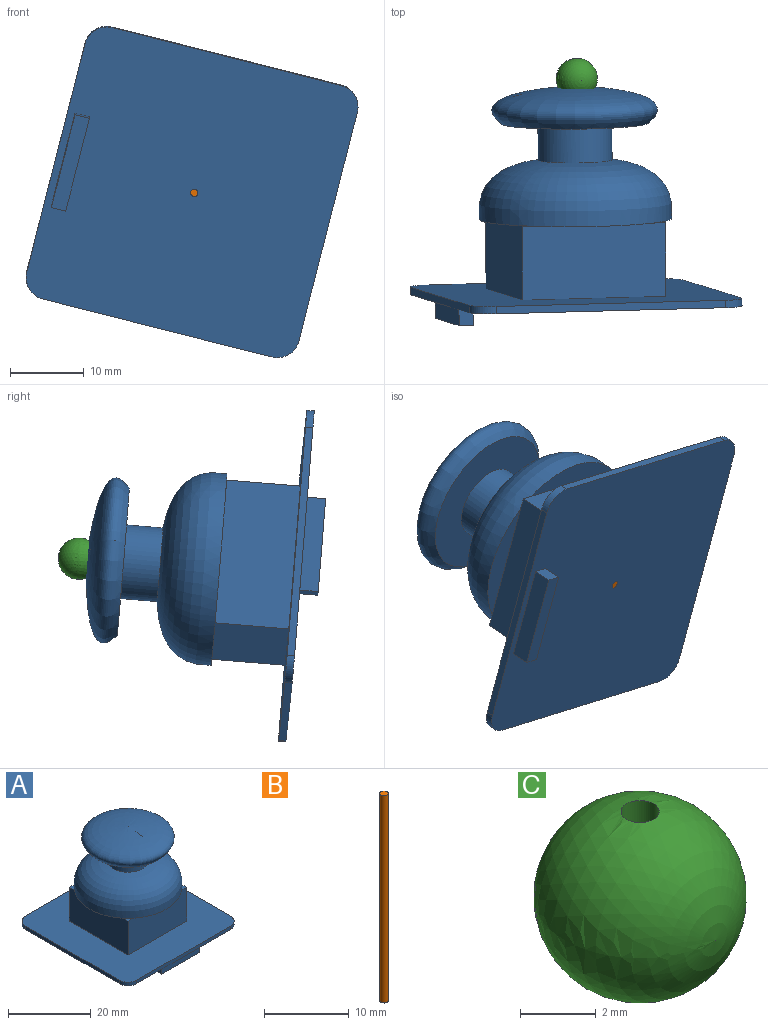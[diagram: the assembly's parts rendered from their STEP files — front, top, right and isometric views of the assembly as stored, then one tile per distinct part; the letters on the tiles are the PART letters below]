
ASSEMBLY  parts=3 mates=2
PART A: 31 faces, bbox 38x38x31.5 mm
  f0: plane 1.69x1.69mm, normal (0,0,1), area 1.3mm2, adj f19,f20,f26
  f1: plane 1.69x1.69mm, normal (0,0,1), area 1.3mm2, adj f20,f21,f26
  f2: plane 1.69x1.69mm, normal (0,0,1), area 1.3mm2, adj f18,f21,f26
  f3: plane 38x38mm, normal (0,0,-1), area 1410.3mm2, adj f4,f5,f6,f7,f9,f10,f11,f12
  f4: plane 32x1mm, normal (0,-1,0), area 32mm2, adj f3,f8,f9,f12
  f5: plane 32x1mm, normal (1,0,0), area 32mm2, adj f3,f8,f9,f10
  f6: plane 32x1mm, normal (0,1,0), area 32mm2, adj f3,f8,f10,f11
  f7: plane 32x1mm, normal (-1,0,0), area 32mm2, adj f3,f8,f11,f12
  f8: plane 38x38mm, normal (0,0,1), area 1036.3mm2, adj f4,f5,f6,f7,f9,f10,f11,f12
  f9: cylinder r=3mm len=3mm, axis (0,0,-1), area 4.7mm2, adj f3,f4,f5,f8
  f10: cylinder r=3mm len=3mm, axis (0,0,1), area 4.7mm2, adj f3,f5,f6,f8
  f11: cylinder r=3mm len=3mm, axis (0,0,-1), area 4.7mm2, adj f3,f6,f7,f8
  f12: cylinder r=3mm len=3mm, axis (0,0,1), area 4.7mm2, adj f3,f4,f7,f8
  f13: plane 13x2.5mm, normal (0,-1,0), area 32.5mm2, adj f3,f14,f16,f17
  f14: plane 2.5x2mm, normal (1,0,0), area 5mm2, adj f3,f13,f15,f17
  f15: plane 13x2.5mm, normal (0,1,0), area 32.5mm2, adj f3,f14,f16,f17
  f16: plane 2.5x2mm, normal (-1,0,0), area 5mm2, adj f3,f13,f15,f17
  f17: plane 13x2mm, normal (0,0,-1), area 26mm2, adj f13,f14,f15,f16
  f18: plane 20x10mm, normal (0,-1,0), area 200mm2, adj f2,f8,f19,f21,f22,f23
  f19: plane 20x10mm, normal (1,0,0), area 200mm2, adj f0,f8,f18,f20,f22,f24
  f20: plane 20x10mm, normal (0,1,0), area 200mm2, adj f0,f1,f8,f19,f21,f25
  f21: plane 20x10mm, normal (-1,0,0), area 200mm2, adj f1,f2,f8,f18,f20,f27
  f22: plane 1.69x1.69mm, normal (0,0,1), area 1.3mm2, adj f18,f19,f26
  f23: plane 16.61x3mm, normal (0,0,-1), area 34.1mm2, adj f18,f26
  f24: plane 16.61x3mm, normal (0,0,-1), area 34.1mm2, adj f19,f26
  f25: plane 16.61x3mm, normal (0,0,-1), area 34.1mm2, adj f20,f26
  f26: revolved ~26.01x26.01mm, area 834.5mm2, adj f0,f1,f2,f22,f23,f24,f25,f27
  f27: plane 16.61x3mm, normal (0,0,-1), area 34.1mm2, adj f21,f26
  f28: revolved ~22.43x22.43mm, area 610.2mm2, adj f29
  f29: plane 20x20mm, normal (0,0,-1), area 235.6mm2, adj f28,f30
  f30: cylinder r=5mm len=10mm, axis (0,0,1), area 157.1mm2, adj f26,f29
PART B: 3 faces, bbox 1x1x30 mm
  f0: cylinder r=0.5mm len=30mm, axis (0,0,-1), area 94.2mm2, adj f1,f2
  f1: plane 1x1mm, normal (0,0,1), area 0.8mm2, adj f0
  f2: plane 1x1mm, normal (0,0,-1), area 0.8mm2, adj f0
PART C: 2 faces, bbox 5.6x5.6x5.6 mm
  f0: sphere r=2.8mm, area 96.9mm2, adj f1
  f1: cylinder r=0.5mm len=5.51mm, axis (0,0,1), area 17.3mm2, adj f0
PLACE A rot(axis=(-0.66,-0.51,-0.55),108.8deg) t=(6.93,11.23,-7.72)mm fixed
PLACE B rot(axis=(0.69,-0.53,0.49),115.5deg) t=(7.04,41.14,-5.33)mm
PLACE C rot(axis=(0.99,0.13,-0.11),95.5deg) t=(2.35,42.62,-23.68)mm
MATE ball A.f3 <-> B.f0  axis (0.01,-1,-0.08) through (7.23,11.24,-7.79)mm
MATE slider B.f0 <-> C.f1  axis (-0.01,1,0.08) through (7.04,41.14,-5.33)mm
